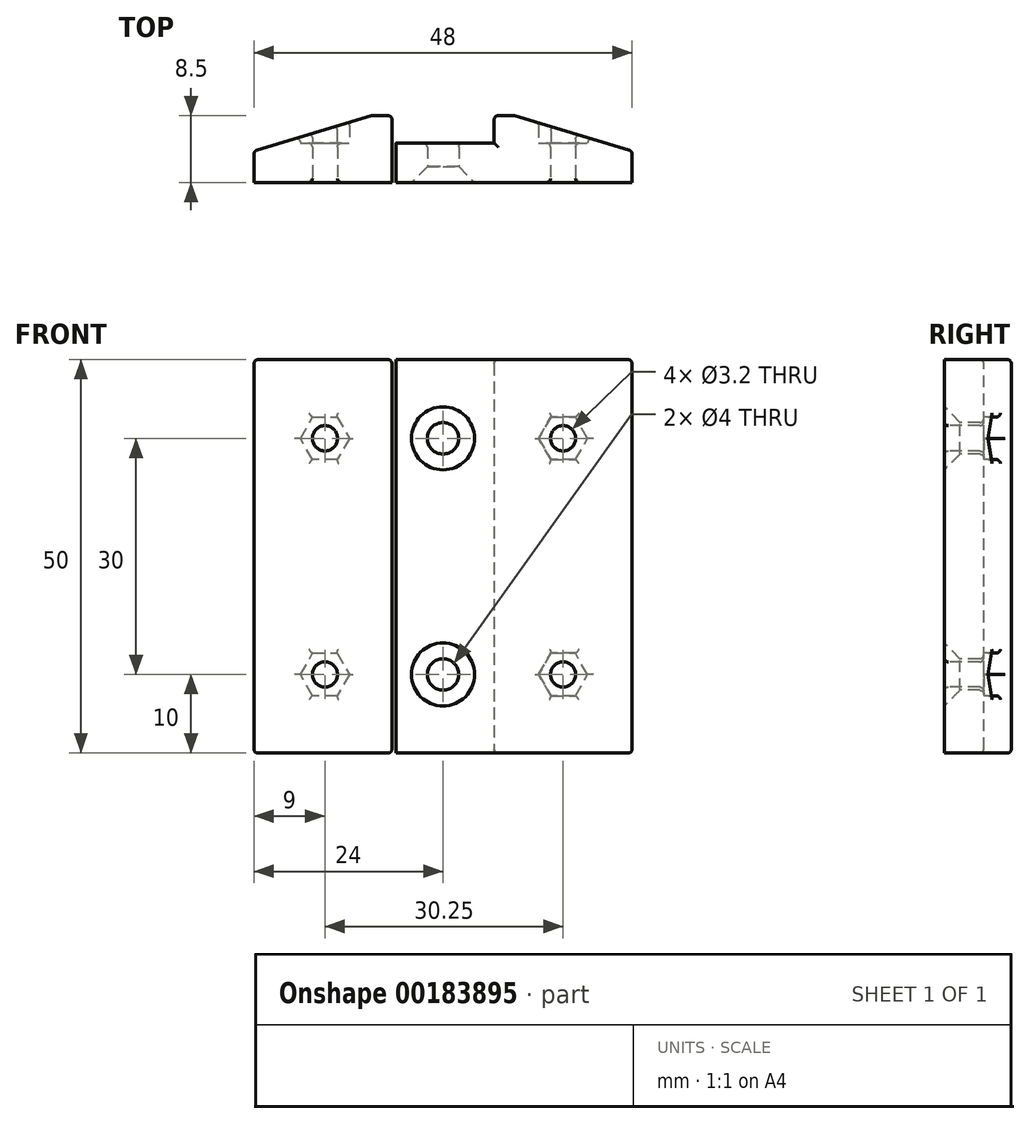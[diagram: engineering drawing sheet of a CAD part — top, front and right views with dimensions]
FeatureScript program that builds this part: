
annotation { "Feature Type Name" : "Feature", "Feature Type Description" : "" }
export const myFeature = defineFeature(function(context is Context, id is Id, definition is map)
    precondition{}
    {
        {
            var Q0;
            Q0=qCreatedBy(makeId("Front.planeOp"),FACE);
            var sketch = newSketch(context, id + "F0", { "sketchPlane" : qUnion([Q0])});
            skLineSegment(sketch, "E0.bottom", {"start": v(6, -25) * mm, "end": v(-6, -25) * mm});
            skLineSegment(sketch, "E0.top", {"start": v(6, 25) * mm, "end": v(-6, 25) * mm});
            skLineSegment(sketch, "E0.left", {"start": v(6, -25) * mm, "end": v(6, 25) * mm});
            skLineSegment(sketch, "E0.right", {"start": v(-6, -25) * mm, "end": v(-6, 25) * mm});
            skPoint(sketch, "E0.middle", {"position": v(0, 0) * mm});
            skLineSegment(sketch, "E1.bottom", {"start": v(-6, 25) * mm, "end": v(-24, 25) * mm});
            skLineSegment(sketch, "E1.top", {"start": v(-6, -25) * mm, "end": v(-24, -25) * mm});
            skLineSegment(sketch, "E1.left", {"start": v(-6, 25) * mm, "end": v(-6, -25) * mm});
            skLineSegment(sketch, "E1.right", {"start": v(-24, 25) * mm, "end": v(-24, -25) * mm});
            skLineSegment(sketch, "E2.MirrorCS", {"start": v(6.5, 25) * mm, "end": v(24, 25) * mm});
            skLineSegment(sketch, "E3.MirrorCS", {"start": v(24, 25) * mm, "end": v(24, -25) * mm});
            skLineSegment(sketch, "E4.MirrorCS", {"start": v(6.5, -25) * mm, "end": v(24, -25) * mm});
            skLineSegment(sketch, "E5.0", {"start": v(-6.5, 25) * mm, "end": v(-6.5, -25) * mm});
            skLineSegment(sketch, "E6.MirrorCS", {"start": v(6.5, 25) * mm, "end": v(6.5, -25) * mm});
            skCircle(sketch, "E7", {"center": v(-15, 15) * mm, "radius": 1.6 * mm});
            skCircle(sketch, "E8.cCircle", {"center": v(-15, 15) * mm, "radius": 2.7 * mm, "construction": true});
            skLineSegment(sketch, "E8.0", {"start": v(-16.56, 17.7) * mm, "end": v(-13.44, 17.7) * mm});
            skLineSegment(sketch, "E8.1", {"start": v(-13.44, 17.7) * mm, "end": v(-11.88, 15) * mm});
            skLineSegment(sketch, "E8.2", {"start": v(-11.88, 15) * mm, "end": v(-13.44, 12.3) * mm});
            skLineSegment(sketch, "E8.3", {"start": v(-13.44, 12.3) * mm, "end": v(-16.56, 12.3) * mm});
            skLineSegment(sketch, "E8.4", {"start": v(-16.56, 12.3) * mm, "end": v(-18.12, 15) * mm});
            skLineSegment(sketch, "E8.5", {"start": v(-18.12, 15) * mm, "end": v(-16.56, 17.7) * mm});
            skPoint(sketch, "E8.0.midPoint", {"position": v(-15, 17.7) * mm});
            skLineSegment(sketch, "E9", {"start": v(-15, 25) * mm, "end": v(-15, -25) * mm, "construction": true});
            skLineSegment(sketch, "E10", {"start": v(0, 25) * mm, "end": v(0, -25) * mm, "construction": true});
            skLineSegment(sketch, "E11", {"start": v(-24, -15) * mm, "end": v(24, -15) * mm, "construction": true});
            skLineSegment(sketch, "E12", {"start": v(-24, 15) * mm, "end": v(24, 15) * mm, "construction": true});
            skCircle(sketch, "E13", {"center": v(-15, -15) * mm, "radius": 1.6 * mm});
            skCircle(sketch, "E14.cCircle", {"center": v(-15, -15) * mm, "radius": 2.7 * mm, "construction": true});
            skLineSegment(sketch, "E14.0", {"start": v(-16.56, -12.3) * mm, "end": v(-13.44, -12.3) * mm});
            skLineSegment(sketch, "E14.1", {"start": v(-13.44, -12.3) * mm, "end": v(-11.88, -15) * mm});
            skLineSegment(sketch, "E14.2", {"start": v(-11.88, -15) * mm, "end": v(-13.44, -17.7) * mm});
            skLineSegment(sketch, "E14.3", {"start": v(-13.44, -17.7) * mm, "end": v(-16.56, -17.7) * mm});
            skLineSegment(sketch, "E14.4", {"start": v(-16.56, -17.7) * mm, "end": v(-18.12, -15) * mm});
            skLineSegment(sketch, "E14.5", {"start": v(-18.12, -15) * mm, "end": v(-16.56, -12.3) * mm});
            skPoint(sketch, "E14.0.midPoint", {"position": v(-15, -12.3) * mm});
            skCircle(sketch, "E15", {"center": v(0, 15) * mm, "radius": 2 * mm});
            skCircle(sketch, "E16", {"center": v(0, -15) * mm, "radius": 2 * mm});
            skLineSegment(sketch, "E17", {"start": v(15.25, 25) * mm, "end": v(15.25, -25) * mm, "construction": true});
            skLineSegment(sketch, "E18", {"start": v(6.5, 25) * mm, "end": v(6, 25) * mm});
            skLineSegment(sketch, "E19", {"start": v(6.5, -25) * mm, "end": v(6, -25) * mm});
            skCircle(sketch, "E20", {"center": v(15.25, 15) * mm, "radius": 1.6 * mm});
            skCircle(sketch, "E21.cCircle", {"center": v(15.25, 15) * mm, "radius": 2.7 * mm, "construction": true});
            skLineSegment(sketch, "E21.0", {"start": v(13.7, 17.7) * mm, "end": v(16.8, 17.7) * mm});
            skLineSegment(sketch, "E21.1", {"start": v(16.8, 17.7) * mm, "end": v(18.37, 15) * mm});
            skLineSegment(sketch, "E21.2", {"start": v(18.37, 15) * mm, "end": v(16.8, 12.3) * mm});
            skLineSegment(sketch, "E21.3", {"start": v(16.8, 12.3) * mm, "end": v(13.7, 12.3) * mm});
            skLineSegment(sketch, "E21.4", {"start": v(13.7, 12.3) * mm, "end": v(12.13, 15) * mm});
            skLineSegment(sketch, "E21.5", {"start": v(12.13, 15) * mm, "end": v(13.7, 17.7) * mm});
            skPoint(sketch, "E21.0.midPoint", {"position": v(15.25, 17.7) * mm});
            skCircle(sketch, "E22", {"center": v(15.25, -15) * mm, "radius": 1.6 * mm});
            skCircle(sketch, "E23.cCircle", {"center": v(15.25, -15) * mm, "radius": 2.7 * mm, "construction": true});
            skLineSegment(sketch, "E23.0", {"start": v(13.7, -12.3) * mm, "end": v(16.8, -12.3) * mm});
            skLineSegment(sketch, "E23.1", {"start": v(16.8, -12.3) * mm, "end": v(18.37, -15) * mm});
            skLineSegment(sketch, "E23.2", {"start": v(18.37, -15) * mm, "end": v(16.8, -17.7) * mm});
            skLineSegment(sketch, "E23.3", {"start": v(16.8, -17.7) * mm, "end": v(13.7, -17.7) * mm});
            skLineSegment(sketch, "E23.4", {"start": v(13.7, -17.7) * mm, "end": v(12.13, -15) * mm});
            skLineSegment(sketch, "E23.5", {"start": v(12.13, -15) * mm, "end": v(13.7, -12.3) * mm});
            skPoint(sketch, "E23.0.midPoint", {"position": v(15.25, -12.3) * mm});
            skSolve(sketch);
        }
        {
            var Q0;
            Q0=makeQuery(id+"F0.imprint","IMPRINT",FACE,{"disambiguationData":[TD([[makeQuery(id+"F0.imprint","IMPRINT",EDGE,{"derivedFrom":sQuery(id+"F0.wireOp",EDGE,"E0.bottom")}),-1.0]])]});
            var Q1;
            {var subQ1=sQuery(id+"F0.wireOp",EDGE,"E1.right");Q1=makeQuery(id+"F0.imprint","IMPRINT",FACE,{"disambiguationData":[TD([[makeQuery(id+"F0.imprint","IMPRINT",EDGE,{"derivedFrom":subQ1}),1.0]])]});}
            var Q2;
            {var subQ0=sQuery(id+"F0.wireOp",EDGE,"E1.left");Q2=makeQuery(id+"F0.imprint","IMPRINT",FACE,{"disambiguationData":[TD([[makeQuery(id+"F0.imprint","IMPRINT",EDGE,{"derivedFrom":subQ0}),-1.0]])]});}
            var Q3;
            Q3=makeQuery(id+"F0.imprint","IMPRINT",FACE,{"disambiguationData":[TD([[makeQuery(id+"F0.imprint","IMPRINT",EDGE,{"derivedFrom":sQuery(id+"F0.wireOp",EDGE,"E0.left")}),-1.0]])]});
            var Q4;
            Q4=makeQuery(id+"F0.imprint","IMPRINT",FACE,{"disambiguationData":[TD([[makeQuery(id+"F0.imprint","IMPRINT",EDGE,{"derivedFrom":sQuery(id+"F0.wireOp",EDGE,"E2.MirrorCS")}),-1.0]])]});
            extrude(context, id + "F1", {"entities" : qUnion([Q0, Q1, Q2, Q3, Q4]), "oppositeDirection" : true, "depth" : 5 * mm});
        }
        {
            var Q0;
            {var subQ0=sQuery(id+"F0.wireOp",EDGE,"E1.right");Q0=makeQuery(id+"F0.imprint","IMPRINT",FACE,{"disambiguationData":[TD([[makeQuery(id+"F0.imprint","IMPRINT",EDGE,{"derivedFrom":subQ0}),1.0]])]});}
            var Q1;
            {var subQ0=sQuery(id+"F0.wireOp",EDGE,"E3.MirrorCS");Q1=makeQuery(id+"F0.imprint","IMPRINT",FACE,{"disambiguationData":[TD([[makeQuery(id+"F0.imprint","IMPRINT",EDGE,{"derivedFrom":subQ0}),-1.0]])]});}
            extrude(context, id + "F2", {"entities" : qUnion([Q0, Q1]), "operationType" : NewBodyOperationType.ADD, "oppositeDirection" : true, "depth" : 8.5 * mm});
        }
        {
            var Q0;
            Q0=makeQuery(id+"F2.opExtrude","CAP_EDGE",EDGE,{"disambiguationData":[OSD([sQuery(id+"F0.wireOp",EDGE,"E1.right")])],"isStart":false});
            chamfer(context, id + "F3", {"entities" : qUnion([Q0]), "chamferType" : ChamferType.TWO_OFFSETS, "width1" : 4.5 * mm, "oppositeDirection" : false, "width2" : 15 * mm});
        }
        {
            var Q0;
            Q0=makeQuery(id+"F2.opExtrude","CAP_EDGE",EDGE,{"disambiguationData":[OSD([sQuery(id+"F0.wireOp",EDGE,"E3.MirrorCS")])],"isStart":false});
            chamfer(context, id + "F4", {"entities" : qUnion([Q0]), "chamferType" : ChamferType.TWO_OFFSETS, "width1" : 4.5 * mm, "oppositeDirection" : true, "width2" : 15 * mm, "tangentPropagation" : true});
        }
        {
            var Q0;
            Q0=sQuery(id+"F0.wireOp",VERTEX,"E15.center");
            var Q1;
            Q1=sQuery(id+"F0.wireOp",VERTEX,"E16.center");
            var Q2;
            Q2=makeQuery(id+"F1.opExtrude","SWEPT_BODY",BODY,{"disambiguationData":[OSD([sQuery(id+"F0.wireOp",EDGE,"E0.bottom"),sQuery(id+"F0.wireOp",EDGE,"E0.top"),sQuery(id+"F0.wireOp",EDGE,"E1.bottom"),sQuery(id+"F0.wireOp",EDGE,"E1.top"),sQuery(id+"F0.wireOp",EDGE,"E1.right"),sQuery(id+"F0.wireOp",EDGE,"E2.MirrorCS"),sQuery(id+"F0.wireOp",EDGE,"E3.MirrorCS"),sQuery(id+"F0.wireOp",EDGE,"E4.MirrorCS")])]});
            hole(context, id + "F5", {"style" : HoleStyle.C_SINK, "endStyle" : HoleEndStyle.THROUGH, "holeDiameter" : 4 * mm, "cSinkDiameter" : 8 * mm, "cSinkAngle" : 90 * degree, "locations" : qUnion([Q0, Q1]), "scope" : qUnion([Q2]), "isTappedThrough" : true});
        }
        {
            var Q0;
            Q0=makeQuery(id+"F0.imprint","IMPRINT",FACE,{"disambiguationData":[TD([[makeQuery(id+"F0.imprint","IMPRINT",EDGE,{"derivedFrom":sQuery(id+"F0.wireOp",EDGE,"E20")}),-1.0]])]});
            var Q1;
            Q1=makeQuery(id+"F0.imprint","IMPRINT",FACE,{"disambiguationData":[TD([[makeQuery(id+"F0.imprint","IMPRINT",EDGE,{"derivedFrom":sQuery(id+"F0.wireOp",EDGE,"E7")}),-1.0]])]});
            var Q2;
            Q2=makeQuery(id+"F0.imprint","IMPRINT",FACE,{"disambiguationData":[TD([[makeQuery(id+"F0.imprint","IMPRINT",EDGE,{"derivedFrom":sQuery(id+"F0.wireOp",EDGE,"E22")}),-1.0]])]});
            var Q3;
            Q3=makeQuery(id+"F0.imprint","IMPRINT",FACE,{"disambiguationData":[TD([[makeQuery(id+"F0.imprint","IMPRINT",EDGE,{"derivedFrom":sQuery(id+"F0.wireOp",EDGE,"E13")}),-1.0]])]});
            extrude(context, id + "F6", {"entities" : qUnion([Q0, Q1, Q2, Q3]), "operationType" : NewBodyOperationType.ADD, "oppositeDirection" : true, "depth" : 5 * mm});
        }
        {
            var Q0;
            Q0=makeQuery(id+"F6.opExtrude","SWEPT_FACE",FACE,{"disambiguationData":[OSD([sQuery(id+"F0.wireOp",EDGE,"E7")])]});
            var Q1;
            Q1=makeQuery(id+"F6.opExtrude","SWEPT_FACE",FACE,{"disambiguationData":[OSD([sQuery(id+"F0.wireOp",EDGE,"E20")])]});
            var Q2;
            Q2=makeQuery(id+"F6.opExtrude","SWEPT_FACE",FACE,{"disambiguationData":[OSD([sQuery(id+"F0.wireOp",EDGE,"E22")])]});
            var Q3;
            Q3=makeQuery(id+"F6.opExtrude","SWEPT_FACE",FACE,{"disambiguationData":[OSD([sQuery(id+"F0.wireOp",EDGE,"E13")])]});
            var Q4;
            Q4=makeQuery(id+"F4.opChamfer","BLEND_FACE",FACE,{"disambiguationData":[OSD([sQuery(id+"F0.wireOp",EDGE,"E3.MirrorCS")])]});
            var Q5;
            Q5=makeQuery(id+"F2.opExtrude","CAP_FACE",FACE,{"disambiguationData":[OSD([sQuery(id+"F0.wireOp",EDGE,"E2.MirrorCS"),sQuery(id+"F0.wireOp",EDGE,"E3.MirrorCS"),sQuery(id+"F0.wireOp",EDGE,"E4.MirrorCS"),sQuery(id+"F0.wireOp",EDGE,"E6.MirrorCS"),sQuery(id+"F0.wireOp",EDGE,"E21.0"),sQuery(id+"F0.wireOp",EDGE,"E21.1"),sQuery(id+"F0.wireOp",EDGE,"E21.2"),sQuery(id+"F0.wireOp",EDGE,"E21.3"),sQuery(id+"F0.wireOp",EDGE,"E21.4"),sQuery(id+"F0.wireOp",EDGE,"E21.5"),sQuery(id+"F0.wireOp",EDGE,"E23.0"),sQuery(id+"F0.wireOp",EDGE,"E23.1"),sQuery(id+"F0.wireOp",EDGE,"E23.2"),sQuery(id+"F0.wireOp",EDGE,"E23.3"),sQuery(id+"F0.wireOp",EDGE,"E23.4"),sQuery(id+"F0.wireOp",EDGE,"E23.5")])],"isStart":false});
            var Q6;
            Q6=makeQuery(id+"F2.opExtrude","CAP_FACE",FACE,{"disambiguationData":[OSD([sQuery(id+"F0.wireOp",EDGE,"E1.bottom"),sQuery(id+"F0.wireOp",EDGE,"E1.top"),sQuery(id+"F0.wireOp",EDGE,"E1.right"),sQuery(id+"F0.wireOp",EDGE,"E5.0"),sQuery(id+"F0.wireOp",EDGE,"E8.0"),sQuery(id+"F0.wireOp",EDGE,"E8.1"),sQuery(id+"F0.wireOp",EDGE,"E8.2"),sQuery(id+"F0.wireOp",EDGE,"E8.3"),sQuery(id+"F0.wireOp",EDGE,"E8.4"),sQuery(id+"F0.wireOp",EDGE,"E8.5"),sQuery(id+"F0.wireOp",EDGE,"E14.0"),sQuery(id+"F0.wireOp",EDGE,"E14.1"),sQuery(id+"F0.wireOp",EDGE,"E14.2"),sQuery(id+"F0.wireOp",EDGE,"E14.3"),sQuery(id+"F0.wireOp",EDGE,"E14.4"),sQuery(id+"F0.wireOp",EDGE,"E14.5")])],"isStart":false});
            var Q7;
            Q7=makeQuery(id+"F3.opChamfer","BLEND_FACE",FACE,{"disambiguationData":[OSD([sQuery(id+"F0.wireOp",EDGE,"E1.right")])]});
            var Q8;
            Q8=makeQuery(id+"F1.opExtrude","CAP_EDGE",EDGE,{"disambiguationData":[OSD([sQuery(id+"F0.wireOp",EDGE,"E16")])],"isStart":false});
            var Q9;
            Q9=makeQuery(id+"F1.opExtrude","CAP_EDGE",EDGE,{"disambiguationData":[OSD([sQuery(id+"F0.wireOp",EDGE,"E15")])],"isStart":false});
            var Q10;
            Q10=makeQuery(id+"F1.opExtrude","CAP_EDGE",EDGE,{"disambiguationData":[OSD([sQuery(id+"F0.wireOp",EDGE,"E0.bottom"),sQuery(id+"F0.wireOp",EDGE,"E1.top"),sQuery(id+"F0.wireOp",EDGE,"E4.MirrorCS"),sQuery(id+"F0.wireOp",EDGE,"E19")])],"isStart":false});
            var Q11;
            Q11=makeQuery(id+"F2.opExtrude","SWEPT_EDGE",EDGE,{"disambiguationData":[OSD([sQuery(id+"F0.wireOp",EDGE,"E4.MirrorCS"),sQuery(id+"F0.wireOp",EDGE,"E6.MirrorCS"),sQuery(id+"F0.wireOp",EDGE,"E19")])]});
            var Q12;
            Q12=makeQuery(id+"F2.opExtrude","SWEPT_EDGE",EDGE,{"disambiguationData":[OSD([sQuery(id+"F0.wireOp",EDGE,"E1.top"),sQuery(id+"F0.wireOp",EDGE,"E5.0")])]});
            var Q13;
            {var subQ0=sQuery(id+"F0.wireOp",EDGE,"E1.right");var subQ1=sQuery(id+"F0.wireOp",EDGE,"E1.top");Q13=makeQuery(id+"F2.boolean.opBoolean","MERGE",EDGE,{"derivedFrom":[makeQuery(id+"F1.opExtrude","SWEPT_EDGE",EDGE,{"disambiguationData":[OSD([subQ1,subQ0])]}),makeQuery(id+"F2.opExtrude","SWEPT_EDGE",EDGE,{"disambiguationData":[OSD([subQ1,subQ0])]})]});}
            var Q14;
            {var subQ0=sQuery(id+"F0.wireOp",EDGE,"E4.MirrorCS");var subQ1=sQuery(id+"F0.wireOp",EDGE,"E3.MirrorCS");Q14=makeQuery(id+"F2.boolean.opBoolean","MERGE",EDGE,{"derivedFrom":[makeQuery(id+"F1.opExtrude","SWEPT_EDGE",EDGE,{"disambiguationData":[OSD([subQ1,subQ0])]}),makeQuery(id+"F2.opExtrude","SWEPT_EDGE",EDGE,{"disambiguationData":[OSD([subQ1,subQ0])]})]});}
            var Q15;
            {var subQ0=sQuery(id+"F0.wireOp",EDGE,"E3.MirrorCS");var subQ1=sQuery(id+"F0.wireOp",EDGE,"E2.MirrorCS");Q15=makeQuery(id+"F2.boolean.opBoolean","MERGE",EDGE,{"derivedFrom":[makeQuery(id+"F1.opExtrude","SWEPT_EDGE",EDGE,{"disambiguationData":[OSD([subQ1,subQ0])]}),makeQuery(id+"F2.opExtrude","SWEPT_EDGE",EDGE,{"disambiguationData":[OSD([subQ1,subQ0])]})]});}
            var Q16;
            Q16=makeQuery(id+"F2.opExtrude","SWEPT_EDGE",EDGE,{"disambiguationData":[OSD([sQuery(id+"F0.wireOp",EDGE,"E2.MirrorCS"),sQuery(id+"F0.wireOp",EDGE,"E6.MirrorCS"),sQuery(id+"F0.wireOp",EDGE,"E18")])]});
            var Q17;
            Q17=makeQuery(id+"F1.opExtrude","CAP_EDGE",EDGE,{"disambiguationData":[OSD([sQuery(id+"F0.wireOp",EDGE,"E0.top"),sQuery(id+"F0.wireOp",EDGE,"E1.bottom"),sQuery(id+"F0.wireOp",EDGE,"E2.MirrorCS"),sQuery(id+"F0.wireOp",EDGE,"E18")])],"isStart":false});
            var Q18;
            Q18=makeQuery(id+"F2.opExtrude","SWEPT_EDGE",EDGE,{"disambiguationData":[OSD([sQuery(id+"F0.wireOp",EDGE,"E1.bottom"),sQuery(id+"F0.wireOp",EDGE,"E5.0")])]});
            var Q19;
            {var subQ0=sQuery(id+"F0.wireOp",EDGE,"E1.right");var subQ1=sQuery(id+"F0.wireOp",EDGE,"E1.bottom");Q19=makeQuery(id+"F2.boolean.opBoolean","MERGE",EDGE,{"derivedFrom":[makeQuery(id+"F1.opExtrude","SWEPT_EDGE",EDGE,{"disambiguationData":[OSD([subQ1,subQ0])]}),makeQuery(id+"F2.opExtrude","SWEPT_EDGE",EDGE,{"disambiguationData":[OSD([subQ1,subQ0])]})]});}
            fillet(context, id + "F7", {"entities" : qUnion([Q0, Q1, Q2, Q3, Q4, Q5, Q6, Q7, Q8, Q9, Q10, Q11, Q12, Q13, Q14, Q15, Q16, Q17, Q18, Q19]), "radius" : 0.5 * mm, "tangentPropagation" : true, "allowEdgeOverflow" : false});
        }
    });
